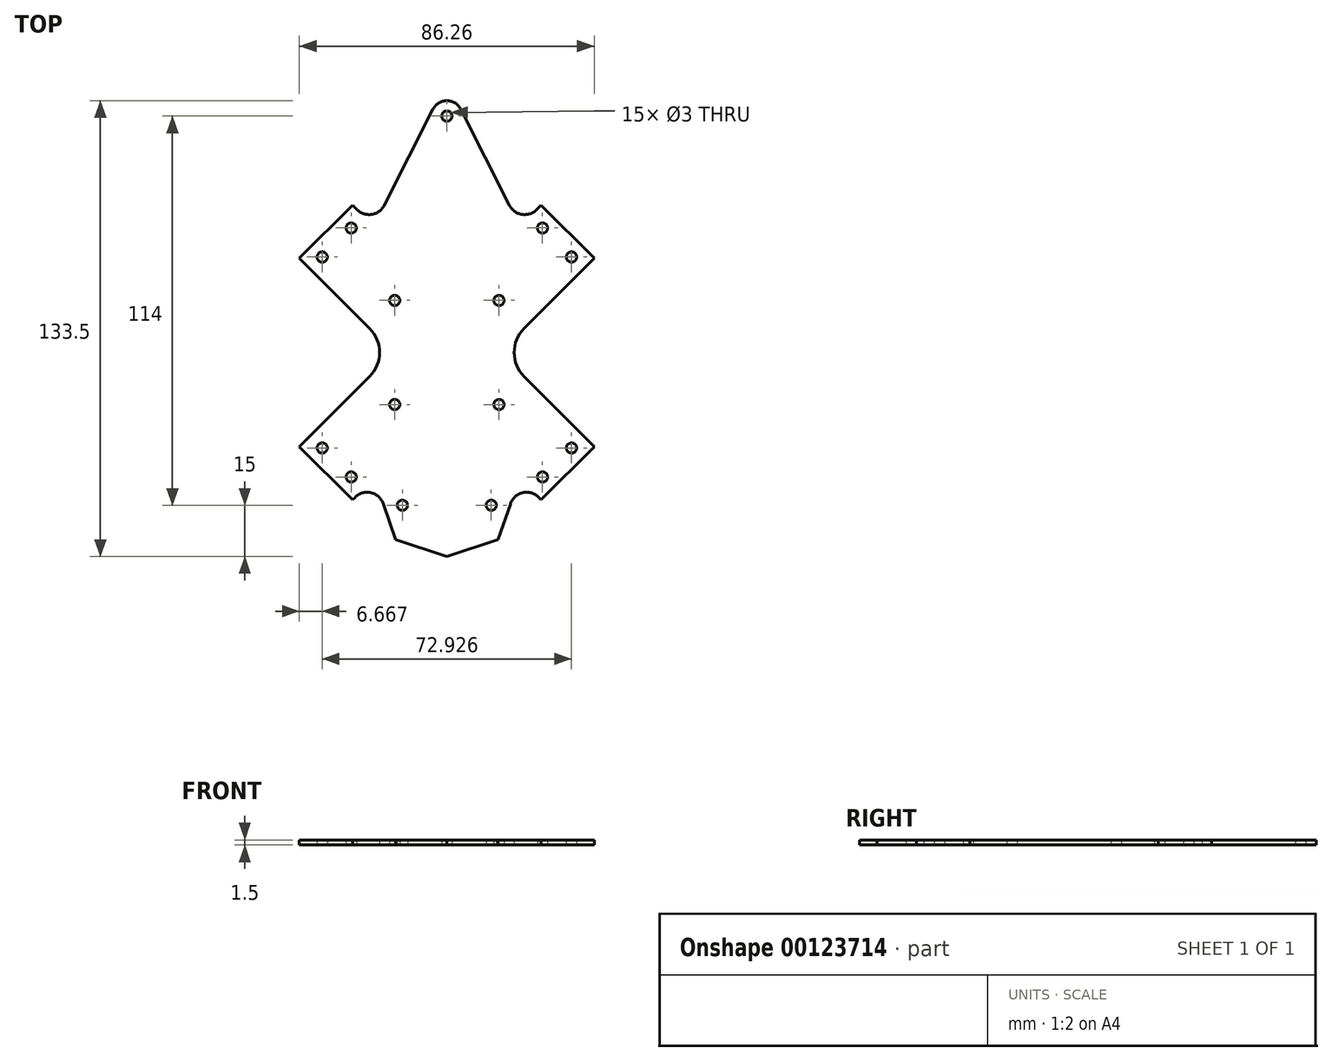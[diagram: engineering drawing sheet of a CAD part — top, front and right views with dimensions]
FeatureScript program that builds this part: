
annotation { "Feature Type Name" : "Feature", "Feature Type Description" : "" }
export const myFeature = defineFeature(function(context is Context, id is Id, definition is map)
    precondition{}
    {
        {
            var Q0;
            Q0=qCreatedBy(makeId("Top.planeOp"),FACE);
            var sketch = newSketch(context, id + "F0", { "sketchPlane" : qUnion([Q0])});
            skCircle(sketch, "E0", {"center": v(-15.25, 15.25) * mm, "radius": 1.5 * mm});
            skCircle(sketch, "E1.0.1.0", {"center": v(-15.25, -15.25) * mm, "radius": 1.5 * mm});
            skCircle(sketch, "E1.1.0.0", {"center": v(15.25, 15.25) * mm, "radius": 1.5 * mm});
            skCircle(sketch, "E1.1.1.0", {"center": v(15.25, -15.25) * mm, "radius": 1.5 * mm});
            skLineSegment(sketch, "E1.direction1", {"start": v(-15.25, 15.25) * mm, "end": v(15.25, 15.25) * mm, "construction": true});
            skLineSegment(sketch, "E1.direction2", {"start": v(-15.25, 15.25) * mm, "end": v(-15.25, -15.25) * mm, "construction": true});
            skLineSegment(sketch, "E2", {"start": v(-42.43, -42.43) * mm, "end": v(42.43, 42.43) * mm, "construction": true});
            skLineSegment(sketch, "E3", {"start": v(-42.43, 42.43) * mm, "end": v(42.43, -42.43) * mm, "construction": true});
            skLineSegment(sketch, "E4", {"start": v(-43.13, 27.58) * mm, "end": v(-27.58, 43.13) * mm});
            skLineSegment(sketch, "E5", {"start": v(-27.58, 43.13) * mm, "end": v(-26.29, 41.84) * mm});
            skPoint(sketch, "E5.endSnap0", {"position": v(0, 15.25) * mm});
            skLineSegment(sketch, "E6", {"start": v(26.29, 41.84) * mm, "end": v(27.58, 43.13) * mm});
            skLineSegment(sketch, "E7", {"start": v(27.58, 43.13) * mm, "end": v(43.13, 27.58) * mm});
            skLineSegment(sketch, "E8", {"start": v(43.13, 27.58) * mm, "end": v(22.63, 7.07) * mm});
            skLineSegment(sketch, "E9", {"start": v(22.63, -7.07) * mm, "end": v(43.13, -27.58) * mm});
            skLineSegment(sketch, "E10", {"start": v(43.13, -27.58) * mm, "end": v(27.58, -43.13) * mm});
            skLineSegment(sketch, "E11", {"start": v(27.58, -43.13) * mm, "end": v(26.86, -42.42) * mm});
            skLineSegment(sketch, "E12", {"start": v(-26.86, -42.42) * mm, "end": v(-27.58, -43.13) * mm});
            skLineSegment(sketch, "E13", {"start": v(-27.58, -43.13) * mm, "end": v(-43.13, -27.58) * mm});
            skLineSegment(sketch, "E14", {"start": v(-43.13, -27.58) * mm, "end": v(-22.63, -7.07) * mm});
            skLineSegment(sketch, "E15", {"start": v(-22.63, 7.07) * mm, "end": v(-43.13, 27.58) * mm});
            skLineSegment(sketch, "E16", {"start": v(-36.46, 27.98) * mm, "end": v(-27.98, 36.46) * mm, "construction": true});
            skLineSegment(sketch, "E17", {"start": v(27.98, 36.46) * mm, "end": v(36.46, 27.98) * mm, "construction": true});
            skLineSegment(sketch, "E18", {"start": v(-36.46, -27.98) * mm, "end": v(-27.98, -36.46) * mm, "construction": true});
            skLineSegment(sketch, "E19", {"start": v(27.98, -36.46) * mm, "end": v(36.46, -27.98) * mm, "construction": true});
            skCircle(sketch, "E20", {"center": v(-36.46, -27.98) * mm, "radius": 1.5 * mm});
            skCircle(sketch, "E21", {"center": v(-27.98, -36.46) * mm, "radius": 1.5 * mm});
            skCircle(sketch, "E22", {"center": v(27.98, -36.46) * mm, "radius": 1.5 * mm});
            skCircle(sketch, "E23", {"center": v(36.46, -27.98) * mm, "radius": 1.5 * mm});
            skCircle(sketch, "E24", {"center": v(36.46, 27.98) * mm, "radius": 1.5 * mm});
            skCircle(sketch, "E25", {"center": v(27.98, 36.46) * mm, "radius": 1.5 * mm});
            skCircle(sketch, "E26", {"center": v(-27.98, 36.46) * mm, "radius": 1.5 * mm});
            skCircle(sketch, "E27", {"center": v(-36.46, 27.98) * mm, "radius": 1.5 * mm});
            skPoint(sketch, "E28.orphan", {"position": v(0, 15.56) * mm});
            skPoint(sketch, "E29.orphan", {"position": v(0, -15.56) * mm});
            skPoint(sketch, "E30.orphan", {"position": v(-15.56, 0) * mm});
            skArc(sketch, "E31", {"start": v(22.63, 7.07) * mm, "mid": v(19.7, 0) * mm, "end": v(22.63, -7.07) * mm});
            skPoint(sketch, "E32.orphan", {"position": v(15.56, 0) * mm});
            skArc(sketch, "E33", {"start": v(-22.63, -7.07) * mm, "mid": v(-19.7, 0) * mm, "end": v(-22.63, 7.07) * mm});
            skCircle(sketch, "E34", {"center": v(0, 69.25) * mm, "radius": 1.5 * mm});
            skArc(sketch, "E35", {"start": v(4.01, 71.28) * mm, "mid": v(0, 73.75) * mm, "end": v(-4.01, 71.28) * mm});
            skLineSegment(sketch, "E36", {"start": v(-4.01, 71.28) * mm, "end": v(-18.3, 43.12) * mm});
            skLineSegment(sketch, "E37", {"start": v(4.01, 71.28) * mm, "end": v(18.3, 43.12) * mm});
            skArc(sketch, "E38", {"start": v(-26.29, 41.84) * mm, "mid": v(-21.96, 40.44) * mm, "end": v(-18.3, 43.12) * mm});
            skPoint(sketch, "E39.start.orphan", {"position": v(-20, 39.75) * mm});
            skArc(sketch, "E40", {"start": v(18.3, 43.12) * mm, "mid": v(21.96, 40.44) * mm, "end": v(26.29, 41.84) * mm});
            skPoint(sketch, "E41.start.orphan", {"position": v(20, 39.75) * mm});
            skLineSegment(sketch, "E42", {"start": v(-13, -44.75) * mm, "end": v(13, -44.75) * mm, "construction": true});
            skCircle(sketch, "E43", {"center": v(-13, -44.75) * mm, "radius": 1.5 * mm});
            skCircle(sketch, "E44", {"center": v(13, -44.75) * mm, "radius": 1.5 * mm});
            skLineSegment(sketch, "E45", {"start": v(-15, -54.75) * mm, "end": v(15, -54.75) * mm, "construction": true});
            skLineSegment(sketch, "E46", {"start": v(-20, -40.25) * mm, "end": v(20, -40.25) * mm, "construction": true});
            skLineSegment(sketch, "E47", {"start": v(-18.6, -44.32) * mm, "end": v(-15, -54.75) * mm});
            skLineSegment(sketch, "E48", {"start": v(0, -59.75) * mm, "end": v(15, -54.75) * mm});
            skLineSegment(sketch, "E49", {"start": v(18.6, -44.32) * mm, "end": v(15, -54.75) * mm});
            skLineSegment(sketch, "E50", {"start": v(-15, -54.75) * mm, "end": v(0, -59.75) * mm});
            skArc(sketch, "E51", {"start": v(-18.6, -44.32) * mm, "mid": v(-22.2, -41.08) * mm, "end": v(-26.86, -42.42) * mm});
            skArc(sketch, "E52", {"start": v(26.86, -42.42) * mm, "mid": v(22.2, -41.08) * mm, "end": v(18.6, -44.32) * mm});
            skSolve(sketch);
        }
        {
            var Q0;
            Q0=qSketchRegion(id+"F0",true);
            extrude(context, id + "F1", {"entities" : qUnion([Q0]), "depth" : 1.5 * mm});
        }
    });
